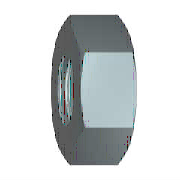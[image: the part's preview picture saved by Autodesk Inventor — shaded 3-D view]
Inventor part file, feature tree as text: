
AUTODESK INVENTOR PART (.ipt)
format: ipt  version: 2015 (Build 190159000, 159)  size: 163,328 bytes
history: native  units: mm (DEFAULTED — no unit token found)
features: sketch x3, other x2, extrude x1, hole x1, plane x1
ambient origin geometry x7: Origin, YZ Plane, XZ Plane, X Axis, Y Axis, Z Axis, Center Point
bodies: Body1 (feature_tree)
feature tree (8):
  extrude  "Bryła"  Depth=18.475209mm
  other  "Faza1"
  hole  "Gwint"  [1 undecoded]
  other  "Work Axis1"
  plane  "Work Plane1"
  sketch  "Szkic1"
  sketch  "Szkic2"
  sketch  "Szkic3"
note: 1 required parameter value undecoded (feature->parameter linkage not recoverable at this tier; creation-order binding heuristic only, values carry confidence <= 0.55)
